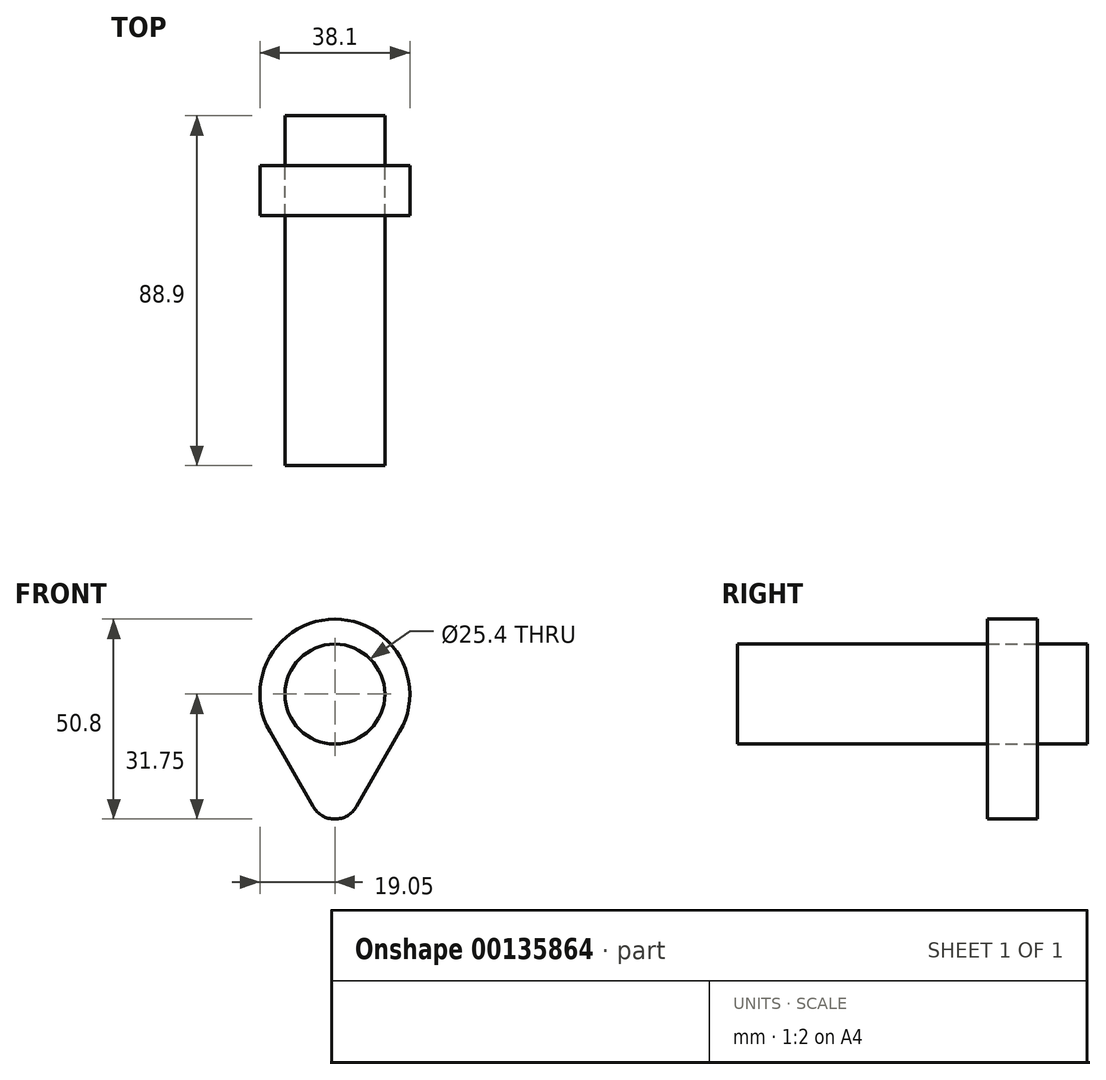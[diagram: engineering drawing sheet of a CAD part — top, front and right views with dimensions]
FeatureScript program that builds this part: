
annotation { "Feature Type Name" : "Feature", "Feature Type Description" : "" }
export const myFeature = defineFeature(function(context is Context, id is Id, definition is map)
    precondition{}
    {
        {
            var Q0;
            Q0=qCreatedBy(makeId("Front.planeOp"),FACE);
            var sketch = newSketch(context, id + "F0", { "sketchPlane" : qUnion([Q0])});
            skCircle(sketch, "E0", {"center": v(0, 0) * mm, "radius": 12.7 * mm});
            skCircle(sketch, "E1", {"center": v(0, 0) * mm, "radius": 19.05 * mm});
            skLineSegment(sketch, "E2", {"start": v(5.5, -28.58) * mm, "end": v(16.5, -9.53) * mm});
            skCircle(sketch, "E3", {"center": v(0, -25.4) * mm, "radius": 6.35 * mm});
            skLineSegment(sketch, "E4", {"start": v(-5.5, -28.58) * mm, "end": v(-16.5, -9.53) * mm});
            skSolve(sketch);
        }
        {
            var Q0;
            {var subQ0=sQuery(id+"F0.wireOp",EDGE,"E2");Q0=makeQuery(id+"F0.imprint","IMPRINT",FACE,{"disambiguationData":[TD([[makeQuery(id+"F0.imprint","IMPRINT",EDGE,{"derivedFrom":subQ0}),1.0]])]});}
            var Q1;
            {var subQ0=sQuery(id+"F0.wireOp",EDGE,"E3");var subQ1=makeQuery(id+"F0.imprint","INTERSECT",VERTEX,{"derivedFrom":[subQ0,sQuery(id+"F0.wireOp",EDGE,"E4")]});Q1=makeQuery(id+"F0.imprint","IMPRINT",FACE,{"disambiguationData":[TD([[makeQuery(id+"F0.imprint","IMPRINT",EDGE,{"disambiguationData":[TD([[subQ1,1.0]])],"derivedFrom":subQ0}),1.0]])]});}
            var Q2;
            Q2=makeQuery(id+"F0.imprint","IMPRINT",FACE,{"disambiguationData":[TD([[makeQuery(id+"F0.imprint","IMPRINT",EDGE,{"derivedFrom":sQuery(id+"F0.wireOp",EDGE,"E0")}),-1.0]])]});
            var Q3;
            {var subQ0=sQuery(id+"F0.wireOp",EDGE,"E4");Q3=makeQuery(id+"F0.imprint","IMPRINT",FACE,{"disambiguationData":[TD([[makeQuery(id+"F0.imprint","IMPRINT",EDGE,{"derivedFrom":subQ0}),-1.0]])]});}
            extrude(context, id + "F1", {"entities" : qUnion([Q0, Q1, Q2, Q3]), "depth" : 12.7 * mm});
        }
        {
            var Q0;
            Q0=qCreatedBy(makeId("Front.planeOp"),FACE);
            var sketch = newSketch(context, id + "F2", { "sketchPlane" : qUnion([Q0])});
            skCircle(sketch, "E5", {"center": v(0, 0) * mm, "radius": 12.7 * mm});
            skSolve(sketch);
        }
        {
            var Q0;
            Q0=makeQuery(id+"F2.imprint","IMPRINT",FACE,{"disambiguationData":[TD([[makeQuery(id+"F2.imprint","IMPRINT",EDGE,{"derivedFrom":sQuery(id+"F2.wireOp",EDGE,"E5")}),1.0]])]});
            extrude(context, id + "F3", {"entities" : qUnion([Q0]), "depth" : 76.2 * mm, "hasSecondDirection" : true, "secondDirectionOppositeDirection" : true, "secondDirectionDepth" : 12.7 * mm});
        }
    });
